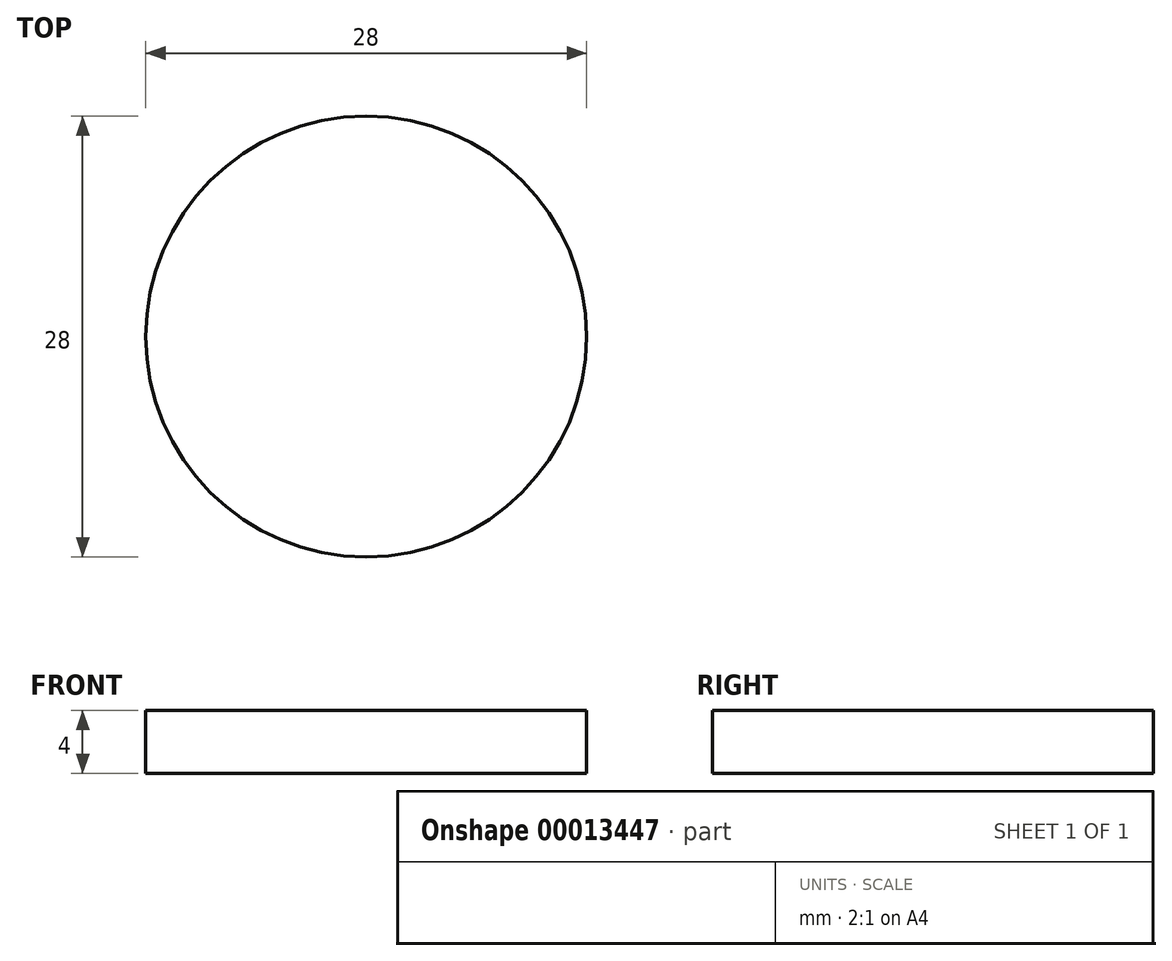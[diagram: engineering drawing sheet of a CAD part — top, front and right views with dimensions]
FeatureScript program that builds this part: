
annotation { "Feature Type Name" : "Feature", "Feature Type Description" : "" }
export const myFeature = defineFeature(function(context is Context, id is Id, definition is map)
    precondition{}
    {
        {
            var Q0;
            Q0=qCreatedBy(makeId("Top.planeOp"),FACE);
            var sketch = newSketch(context, id + "F0", { "sketchPlane" : qUnion([Q0])});
            skCircle(sketch, "E0", {"center": v(0, 0) * mm, "radius": 14 * mm});
            skSolve(sketch);
        }
        {
            var Q0;
            Q0=qSketchRegion(id+"F0",true);
            extrude(context, id + "F1", {"entities" : qUnion([Q0]), "depth" : 4 * mm});
        }
    });
